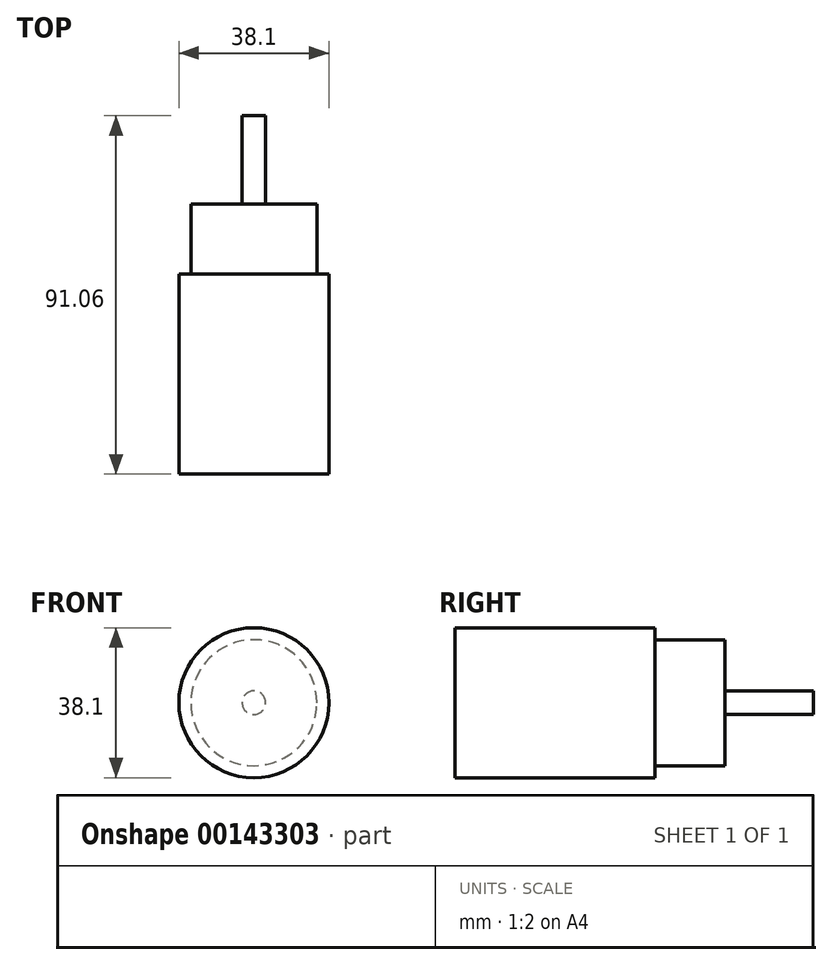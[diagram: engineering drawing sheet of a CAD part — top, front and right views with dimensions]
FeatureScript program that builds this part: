
annotation { "Feature Type Name" : "Feature", "Feature Type Description" : "" }
export const myFeature = defineFeature(function(context is Context, id is Id, definition is map)
    precondition{}
    {
        {
            var Q0;
            Q0=qCreatedBy(makeId("Front.planeOp"),FACE);
            var sketch = newSketch(context, id + "F0", { "sketchPlane" : qUnion([Q0])});
            skCircle(sketch, "E0", {"center": v(0, 0) * mm, "radius": 16 * mm});
            skSolve(sketch);
        }
        {
            var Q0;
            Q0 = qSketchRegion(id + "F0", true);
            extrude(context, id + "F1", {"entities" : qUnion([Q0]), "depth" : 17.78 * mm});
        }
        {
            var Q0;
            Q0=makeQuery(id+"F1.opExtrude","CAP_FACE",FACE,{"disambiguationData":[OSD([sQuery(id+"F0.wireOp",EDGE,"E0")])],"isStart":false});
            var sketch = newSketch(context, id + "F2", { "sketchPlane" : qUnion([Q0])});
            skCircle(sketch, "E1", {"center": v(0, 0) * mm, "radius": 19.05 * mm});
            skSolve(sketch);
        }
        {
            var Q0;
            Q0 = qSketchRegion(id + "F2", true);
            extrude(context, id + "F3", {"entities" : qUnion([Q0]), "operationType" : NewBodyOperationType.ADD, "depth" : 50.8 * mm});
        }
        {
            var Q0;
            Q0=makeQuery(id+"F1.opExtrude","CAP_FACE",FACE,{"disambiguationData":[OSD([sQuery(id+"F0.wireOp",EDGE,"E0")])],"isStart":true});
            var sketch = newSketch(context, id + "F4", { "sketchPlane" : qUnion([Q0])});
            skLineSegment(sketch, "E2", {"start": v(0, -16) * mm, "end": v(0, 0) * mm});
            skLineSegment(sketch, "E3", {"start": v(0, 0) * mm, "end": v(0, -16) * mm});
            skCircle(sketch, "E4", {"center": v(0, 0) * mm, "radius": 3 * mm});
            skSolve(sketch);
        }
        {
            var Q0;
            Q0 = qSketchRegion(id + "F4", true);
            extrude(context, id + "F5", {"entities" : qUnion([Q0]), "operationType" : NewBodyOperationType.ADD, "depth" : 22.48 * mm});
        }
    });
